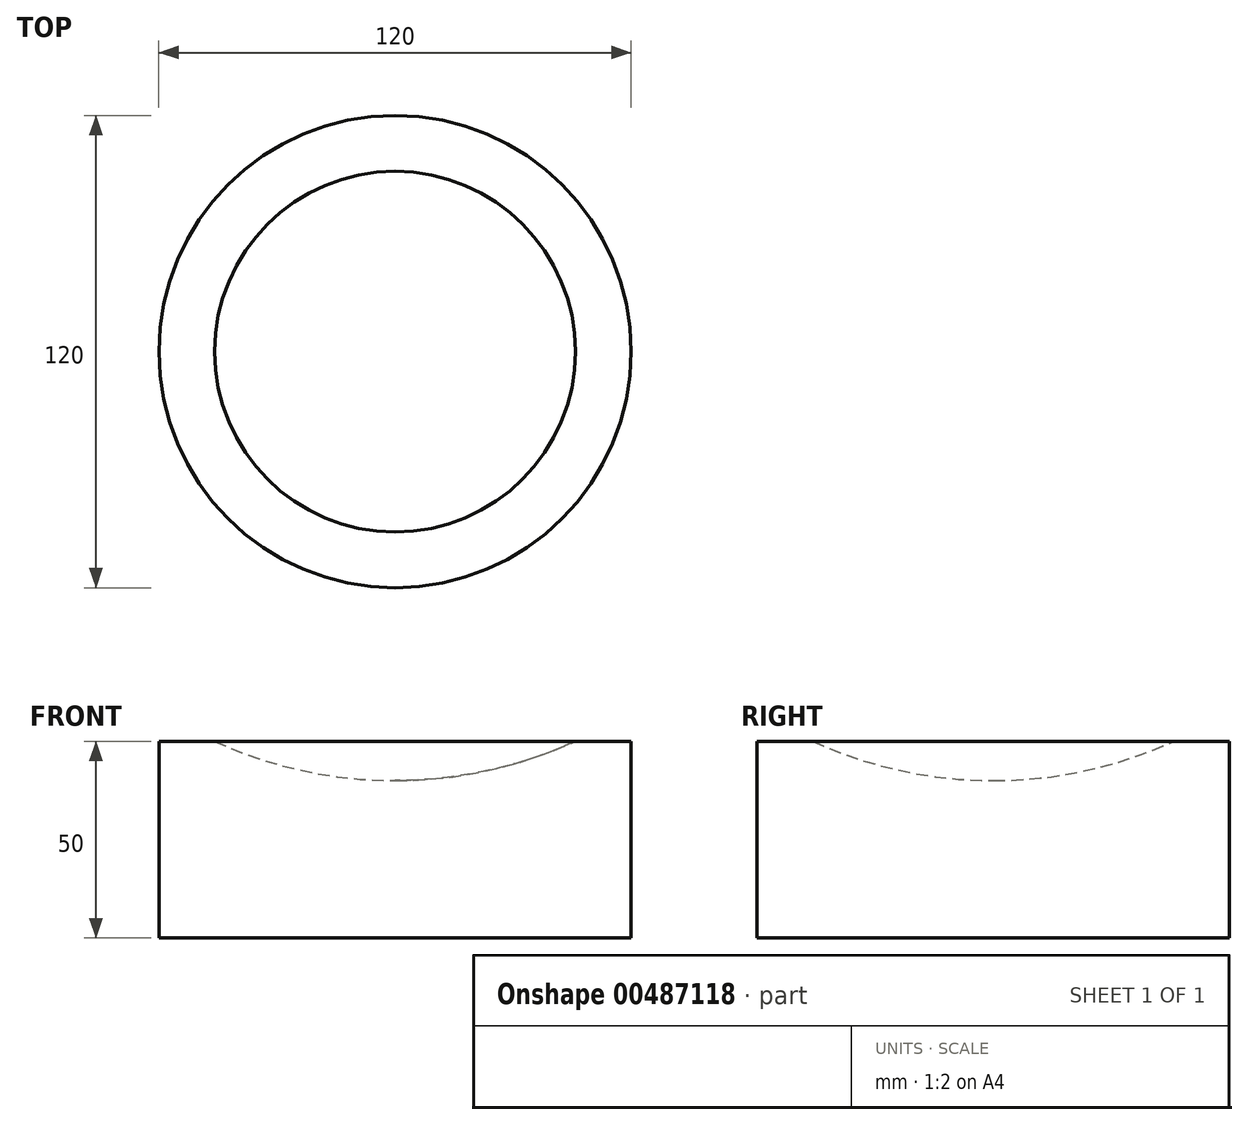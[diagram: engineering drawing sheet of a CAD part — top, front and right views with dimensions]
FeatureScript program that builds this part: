
annotation { "Feature Type Name" : "Feature", "Feature Type Description" : "" }
export const myFeature = defineFeature(function(context is Context, id is Id, definition is map)
    precondition{}
    {
        {
            var Q0;
            Q0=qCreatedBy(makeId("Front.planeOp"),FACE);
            var sketch = newSketch(context, id + "F0", { "sketchPlane" : qUnion([Q0])});
            skLineSegment(sketch, "E0.bottom", {"start": v(-28.35, 0) * mm, "end": v(31.65, 0) * mm});
            skLineSegment(sketch, "E0.top", {"start": v(17.48, 50) * mm, "end": v(31.65, 50) * mm});
            skLineSegment(sketch, "E0.left", {"start": v(-28.35, 0) * mm, "end": v(-28.35, 40) * mm});
            skLineSegment(sketch, "E0.right", {"start": v(31.65, 0) * mm, "end": v(31.65, 50) * mm});
            skArc(sketch, "E1", {"start": v(-28.35, 40) * mm, "mid": v(-4.9, 42.53) * mm, "end": v(17.48, 50) * mm});
            skPoint(sketch, "E2.orphan", {"position": v(-28.35, 50) * mm});
            skSolve(sketch);
        }
        {
            var Q0;
            Q0=makeQuery(id+"F0.imprint","IMPRINT",FACE,{"disambiguationData":[TD([[makeQuery(id+"F0.imprint","IMPRINT",EDGE,{"derivedFrom":sQuery(id+"F0.wireOp",EDGE,"E0.bottom")}),1.0]])]});
            var Q1;
            Q1=sQuery(id+"F0.wireOp",EDGE,"E0.left");
            revolve(context, id + "F1", {"entities" : qUnion([Q0]), "axis" : qUnion([Q1]), "revolveType" : RevolveType.FULL});
        }
    });
